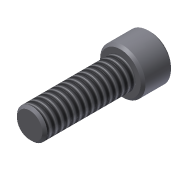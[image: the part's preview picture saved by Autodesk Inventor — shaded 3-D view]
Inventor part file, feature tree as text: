
AUTODESK INVENTOR PART (.ipt)
format: ipt  version: 2013 (Build 170138000, 138)  size: 112,128 bytes
history: native  units: in
note: dims shown in document units (in); Inventor stores cm internally (conversion verified against a paired STEP export)
features: extrude x3, sketch x3, chamfer x1, thread x1
ambient origin geometry x8: Origin, YZ Plane, XZ Plane, XY Plane, X Axis, Y Axis, Z Axis, Center Point
bodies: Solid1 (feature_tree)
feature tree (8):
  extrude  "Extrusion1"  Depth=0.75in TaperAngle=0.0deg
  extrude  "Extrusion2"  Depth=0.25in TaperAngle=0.0deg
  extrude  "Extrusion3"  Depth=0.125in TaperAngle=0.0deg
  chamfer  "Chamfer1"  Distance=0.02in Angle=45.0deg
  thread  "Thread1"  [1 undecoded]
  sketch  "Sketch1"  dims[d0=0.25in d1=0.75in d2=0.0in]
  sketch  "Sketch2"  dims[d3=0.375in d4=0.25in d5=0.0in]
  sketch  "Sketch3"  dims[d6=0.1875in d7=0.125in d8=0.0in d9=0.02in d10=0.125in d11=45.0deg d12=1.0in d13=0.0in]
note: 1 required parameter value undecoded (feature->parameter linkage not recoverable at this tier; creation-order binding heuristic only, values carry confidence <= 0.55)
